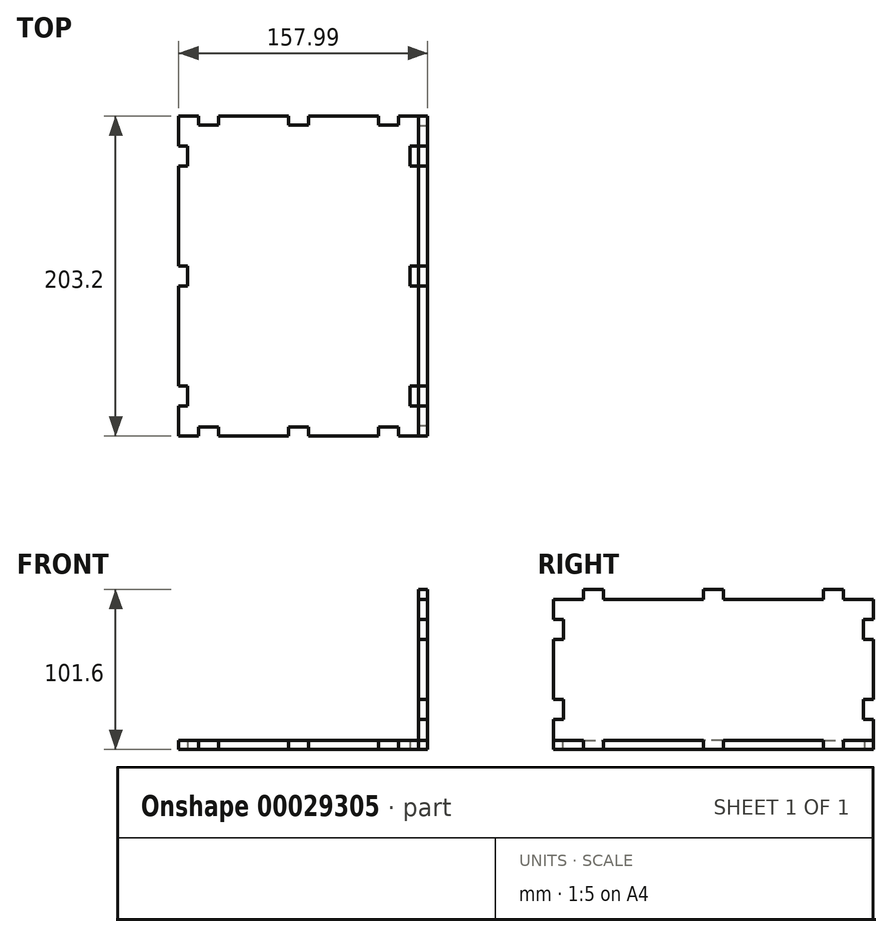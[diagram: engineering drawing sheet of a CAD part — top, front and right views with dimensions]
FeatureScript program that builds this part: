
annotation { "Feature Type Name" : "Feature", "Feature Type Description" : "" }
export const myFeature = defineFeature(function(context is Context, id is Id, definition is map)
    precondition{}
    {
        {
            var Q0;
            Q0=qCreatedBy(makeId("Top.planeOp"),FACE);
            var sketch = newSketch(context, id + "F0", { "sketchPlane" : qUnion([Q0])});
            skLineSegment(sketch, "E0", {"start": v(0, -101.6) * mm, "end": v(0, 101.6) * mm, "construction": true});
            skLineSegment(sketch, "E1", {"start": v(-76.2, 0) * mm, "end": v(76.2, 0) * mm, "construction": true});
            skLineSegment(sketch, "E2.0", {"start": v(38.1, -101.6) * mm, "end": v(38.1, 101.6) * mm, "construction": true});
            skLineSegment(sketch, "E3.0", {"start": v(76.2, -101.6) * mm, "end": v(76.2, -82.55) * mm, "construction": true});
            skLineSegment(sketch, "E4.0", {"start": v(-38.1, -101.6) * mm, "end": v(-38.1, 101.6) * mm, "construction": true});
            skLineSegment(sketch, "E5.0", {"start": v(-76.2, -101.6) * mm, "end": v(-76.2, 76.2) * mm, "construction": true});
            skLineSegment(sketch, "E6.0", {"start": v(-76.2, -50.8) * mm, "end": v(76.2, -50.8) * mm, "construction": true});
            skLineSegment(sketch, "E7.0", {"start": v(-76.2, -101.6) * mm, "end": v(-63.5, -101.6) * mm, "construction": true});
            skLineSegment(sketch, "E8.0", {"start": v(-76.2, 50.8) * mm, "end": v(76.2, 50.8) * mm, "construction": true});
            skLineSegment(sketch, "E9.0", {"start": v(-76.2, 101.6) * mm, "end": v(76.2, 101.6) * mm, "construction": true});
            skLineSegment(sketch, "E10.bottom", {"start": v(-76.2, -101.6) * mm, "end": v(-63.5, -101.6) * mm});
            skLineSegment(sketch, "E10.top", {"start": v(-76.2, 101.6) * mm, "end": v(-63.5, 101.6) * mm});
            skLineSegment(sketch, "E10.left", {"start": v(-76.2, -101.6) * mm, "end": v(-76.2, -82.55) * mm});
            skLineSegment(sketch, "E10.right", {"start": v(76.2, -101.6) * mm, "end": v(76.2, -82.55) * mm});
            skLineSegment(sketch, "E11.0", {"start": v(-57.15, -101.6) * mm, "end": v(-57.15, 101.6) * mm, "construction": true});
            skLineSegment(sketch, "E12.0", {"start": v(57.15, -101.6) * mm, "end": v(57.15, 101.6) * mm, "construction": true});
            skLineSegment(sketch, "E13.0", {"start": v(-76.2, -76.2) * mm, "end": v(76.2, -76.2) * mm, "construction": true});
            skLineSegment(sketch, "E14.0", {"start": v(-76.2, 76.2) * mm, "end": v(76.2, 76.2) * mm, "construction": true});
            skLineSegment(sketch, "E15.0", {"start": v(-76.2, -69.85) * mm, "end": v(76.2, -69.85) * mm, "construction": true});
            skLineSegment(sketch, "E16.0", {"start": v(-76.2, -82.55) * mm, "end": v(76.2, -82.55) * mm, "construction": true});
            skLineSegment(sketch, "E17.0", {"start": v(-70.61, -101.6) * mm, "end": v(-70.61, 101.6) * mm, "construction": true});
            skLineSegment(sketch, "E18.0", {"start": v(-76.2, -96.01) * mm, "end": v(76.2, -96.01) * mm, "construction": true});
            skLineSegment(sketch, "E19.0", {"start": v(-76.2, 96.01) * mm, "end": v(76.2, 96.01) * mm, "construction": true});
            skLineSegment(sketch, "E20.0", {"start": v(70.61, -101.6) * mm, "end": v(70.61, 101.6) * mm, "construction": true});
            skLineSegment(sketch, "E21", {"start": v(-76.2, -82.55) * mm, "end": v(-70.61, -82.55) * mm});
            skLineSegment(sketch, "E22", {"start": v(-70.61, -82.55) * mm, "end": v(-70.61, -69.85) * mm});
            skLineSegment(sketch, "E23", {"start": v(-70.61, -69.85) * mm, "end": v(-76.2, -69.85) * mm});
            skLineSegment(sketch, "E24", {"start": v(76.2, -82.55) * mm, "end": v(70.61, -82.55) * mm});
            skLineSegment(sketch, "E25", {"start": v(70.61, -82.55) * mm, "end": v(70.61, -69.85) * mm});
            skLineSegment(sketch, "E26", {"start": v(70.61, -69.85) * mm, "end": v(76.2, -69.85) * mm});
            skLineSegment(sketch, "E27.0", {"start": v(-76.2, 6.35) * mm, "end": v(76.2, 6.35) * mm, "construction": true});
            skLineSegment(sketch, "E28.0", {"start": v(-76.2, -6.35) * mm, "end": v(76.2, -6.35) * mm, "construction": true});
            skLineSegment(sketch, "E29", {"start": v(-76.2, -6.35) * mm, "end": v(-70.61, -6.35) * mm});
            skLineSegment(sketch, "E30.0", {"start": v(-76.2, 82.55) * mm, "end": v(76.2, 82.55) * mm, "construction": true});
            skLineSegment(sketch, "E31.0", {"start": v(-76.2, 69.85) * mm, "end": v(76.2, 69.85) * mm, "construction": true});
            skLineSegment(sketch, "E32", {"start": v(-70.61, -6.35) * mm, "end": v(-70.61, 6.35) * mm});
            skLineSegment(sketch, "E33", {"start": v(-70.61, 6.35) * mm, "end": v(-76.2, 6.35) * mm});
            skLineSegment(sketch, "E34", {"start": v(-76.2, 69.85) * mm, "end": v(-70.61, 69.85) * mm});
            skLineSegment(sketch, "E35", {"start": v(-70.61, 69.85) * mm, "end": v(-70.61, 82.55) * mm});
            skLineSegment(sketch, "E36", {"start": v(-70.61, 82.55) * mm, "end": v(-76.2, 82.55) * mm});
            skLineSegment(sketch, "E37", {"start": v(76.2, 69.85) * mm, "end": v(70.61, 69.85) * mm});
            skLineSegment(sketch, "E38", {"start": v(70.61, 69.85) * mm, "end": v(70.61, 82.55) * mm});
            skLineSegment(sketch, "E39", {"start": v(70.61, 82.55) * mm, "end": v(76.2, 82.55) * mm});
            skLineSegment(sketch, "E40", {"start": v(76.2, 6.35) * mm, "end": v(70.61, 6.35) * mm});
            skLineSegment(sketch, "E41", {"start": v(70.61, 6.35) * mm, "end": v(70.61, -6.35) * mm});
            skLineSegment(sketch, "E42", {"start": v(70.61, -6.35) * mm, "end": v(76.2, -6.35) * mm});
            skLineSegment(sketch, "E43.0", {"start": v(-63.5, -101.6) * mm, "end": v(-63.5, 101.6) * mm, "construction": true});
            skLineSegment(sketch, "E44.0", {"start": v(-50.8, -101.6) * mm, "end": v(-50.8, 101.6) * mm, "construction": true});
            skLineSegment(sketch, "E45.0", {"start": v(-6.35, -101.6) * mm, "end": v(-6.35, 101.6) * mm, "construction": true});
            skLineSegment(sketch, "E46.0", {"start": v(6.35, -101.6) * mm, "end": v(6.35, 101.6) * mm, "construction": true});
            skLineSegment(sketch, "E47.0", {"start": v(50.8, -101.6) * mm, "end": v(50.8, 101.6) * mm, "construction": true});
            skLineSegment(sketch, "E48.0", {"start": v(63.5, -101.6) * mm, "end": v(63.5, 101.6) * mm, "construction": true});
            skLineSegment(sketch, "E49", {"start": v(-63.5, -101.6) * mm, "end": v(-63.5, -96.01) * mm});
            skLineSegment(sketch, "E50", {"start": v(-63.5, -96.01) * mm, "end": v(-50.8, -96.01) * mm});
            skLineSegment(sketch, "E51", {"start": v(-50.8, -96.01) * mm, "end": v(-50.8, -101.6) * mm});
            skLineSegment(sketch, "E52", {"start": v(-6.35, -101.6) * mm, "end": v(-6.35, -96.01) * mm});
            skLineSegment(sketch, "E53", {"start": v(-6.35, -96.01) * mm, "end": v(6.35, -96.01) * mm});
            skLineSegment(sketch, "E54", {"start": v(6.35, -96.01) * mm, "end": v(6.35, -101.6) * mm});
            skLineSegment(sketch, "E55", {"start": v(50.8, -101.6) * mm, "end": v(50.8, -96.01) * mm});
            skLineSegment(sketch, "E56", {"start": v(50.8, -96.01) * mm, "end": v(63.5, -96.01) * mm});
            skLineSegment(sketch, "E57", {"start": v(63.5, -96.01) * mm, "end": v(63.5, -101.6) * mm});
            skLineSegment(sketch, "E58.trimOffspring", {"start": v(63.5, -101.6) * mm, "end": v(76.2, -101.6) * mm});
            skLineSegment(sketch, "E59.trimOffspring", {"start": v(76.2, -69.85) * mm, "end": v(76.2, -6.35) * mm});
            skLineSegment(sketch, "E60.trimOffspring", {"start": v(76.2, -69.85) * mm, "end": v(76.2, -6.35) * mm, "construction": true});
            skLineSegment(sketch, "E61.trimOffspring", {"start": v(76.2, 6.35) * mm, "end": v(76.2, 69.85) * mm});
            skLineSegment(sketch, "E62.trimOffspring", {"start": v(76.2, 6.35) * mm, "end": v(76.2, 69.85) * mm, "construction": true});
            skLineSegment(sketch, "E63.trimOffspring", {"start": v(76.2, 82.55) * mm, "end": v(76.2, 101.6) * mm});
            skLineSegment(sketch, "E64.trimOffspring", {"start": v(76.2, 82.55) * mm, "end": v(76.2, 101.6) * mm, "construction": true});
            skLineSegment(sketch, "E65.trimOffspring", {"start": v(-76.2, 82.55) * mm, "end": v(-76.2, 101.6) * mm});
            skLineSegment(sketch, "E66.trimOffspring", {"start": v(-76.2, 82.55) * mm, "end": v(-76.2, 101.6) * mm, "construction": true});
            skLineSegment(sketch, "E67.trimOffspring", {"start": v(-76.2, 6.35) * mm, "end": v(-76.2, 69.85) * mm});
            skLineSegment(sketch, "E68.trimOffspring", {"start": v(-76.2, -69.85) * mm, "end": v(-76.2, -6.35) * mm});
            skLineSegment(sketch, "E69.trimOffspring", {"start": v(-50.8, -101.6) * mm, "end": v(-6.35, -101.6) * mm});
            skLineSegment(sketch, "E70.trimOffspring", {"start": v(-57.15, -101.6) * mm, "end": v(76.2, -101.6) * mm, "construction": true});
            skLineSegment(sketch, "E71.trimOffspring", {"start": v(6.35, -101.6) * mm, "end": v(50.8, -101.6) * mm});
            skLineSegment(sketch, "E72", {"start": v(-63.5, 101.6) * mm, "end": v(-63.5, 96.01) * mm});
            skLineSegment(sketch, "E73", {"start": v(-63.5, 96.01) * mm, "end": v(-50.8, 96.01) * mm});
            skLineSegment(sketch, "E74", {"start": v(-50.8, 96.01) * mm, "end": v(-50.8, 101.6) * mm});
            skLineSegment(sketch, "E75", {"start": v(-6.35, 101.6) * mm, "end": v(-6.35, 96.01) * mm});
            skLineSegment(sketch, "E76", {"start": v(-6.35, 96.01) * mm, "end": v(6.35, 96.01) * mm});
            skLineSegment(sketch, "E77", {"start": v(6.35, 96.01) * mm, "end": v(6.35, 101.6) * mm});
            skLineSegment(sketch, "E78", {"start": v(50.8, 101.6) * mm, "end": v(50.8, 96.01) * mm});
            skLineSegment(sketch, "E79", {"start": v(50.8, 96.01) * mm, "end": v(63.5, 96.01) * mm});
            skLineSegment(sketch, "E80", {"start": v(63.5, 96.01) * mm, "end": v(63.5, 101.6) * mm});
            skLineSegment(sketch, "E81.trimOffspring", {"start": v(63.5, 101.6) * mm, "end": v(76.2, 101.6) * mm});
            skLineSegment(sketch, "E82.trimOffspring", {"start": v(6.35, 101.6) * mm, "end": v(50.8, 101.6) * mm});
            skLineSegment(sketch, "E83.trimOffspring", {"start": v(-50.8, 101.6) * mm, "end": v(-6.35, 101.6) * mm});
            skSolve(sketch);
        }
        {
            var Q0;
            Q0=makeQuery(id+"F0.imprint","IMPRINT",FACE,{"disambiguationData":[TD([[makeQuery(id+"F0.imprint","IMPRINT",EDGE,{"derivedFrom":sQuery(id+"F0.wireOp",EDGE,"E10.bottom")}),1.0]])]});
            extrude(context, id + "F1", {"entities" : qUnion([Q0]), "depth" : 5.6 * mm});
        }
        {
            var Q0;
            Q0=qCreatedBy(makeId("Right.planeOp"),FACE);
            cPlane(context, id + "F2", {"entities" : qUnion([Q0]), "cplaneType" : CPlaneType.OFFSET, "offset" : 76.2 * mm, "width" : 152.4 * mm, "height" : 152.4 * mm});
        }
        {
            var Q0;
            Q0=qCreatedBy(id+"F2.planeOp",FACE);
            var sketch = newSketch(context, id + "F3", { "sketchPlane" : qUnion([Q0])});
            skLineSegment(sketch, "E84", {"start": v(0, 0) * mm, "end": v(0, 101.6) * mm, "construction": true});
            skLineSegment(sketch, "E85", {"start": v(0, 50.8) * mm, "end": v(-101.6, 50.8) * mm, "construction": true});
            skLineSegment(sketch, "E86", {"start": v(0, 50.8) * mm, "end": v(101.6, 50.8) * mm, "construction": true});
            skPoint(sketch, "E87.0", {"position": v(-76.2, 0) * mm});
            skPoint(sketch, "E88.0", {"position": v(76.2, 0) * mm});
            skLineSegment(sketch, "E89.0", {"start": v(0, 101.6) * mm, "end": v(-101.6, 101.6) * mm, "construction": true});
            skLineSegment(sketch, "E90.0", {"start": v(0, 101.6) * mm, "end": v(101.6, 101.6) * mm, "construction": true});
            skLineSegment(sketch, "E91.0", {"start": v(101.6, 0) * mm, "end": v(101.6, 101.6) * mm, "construction": true});
            skLineSegment(sketch, "E92.0", {"start": v(-101.6, 0) * mm, "end": v(-101.6, 101.6) * mm, "construction": true});
            skLineSegment(sketch, "E93.0", {"start": v(0, 0) * mm, "end": v(-101.6, 0) * mm, "construction": true});
            skLineSegment(sketch, "E94.0", {"start": v(0, 0) * mm, "end": v(101.6, 0) * mm, "construction": true});
            skLineSegment(sketch, "E95.0", {"start": v(0, 25.4) * mm, "end": v(101.6, 25.4) * mm, "construction": true});
            skLineSegment(sketch, "E96.0", {"start": v(0, 76.2) * mm, "end": v(101.6, 76.2) * mm, "construction": true});
            skLineSegment(sketch, "E97.0", {"start": v(0, 76.2) * mm, "end": v(-101.6, 76.2) * mm, "construction": true});
            skLineSegment(sketch, "E98.0", {"start": v(0, 25.4) * mm, "end": v(-101.6, 25.4) * mm, "construction": true});
            skLineSegment(sketch, "E99.0", {"start": v(-101.6, 5.59) * mm, "end": v(-82.55, 5.59) * mm});
            skLineSegment(sketch, "E100.0", {"start": v(-82.55, 5.59) * mm, "end": v(-82.55, 0) * mm});
            skLineSegment(sketch, "E101.0", {"start": v(-69.85, 5.59) * mm, "end": v(-69.85, 0) * mm});
            skLineSegment(sketch, "E102.0", {"start": v(-69.85, 5.59) * mm, "end": v(-6.35, 5.59) * mm});
            skLineSegment(sketch, "E103.0", {"start": v(-6.35, 5.59) * mm, "end": v(-6.35, 0) * mm});
            skLineSegment(sketch, "E104.0", {"start": v(6.35, 5.59) * mm, "end": v(6.35, 0) * mm});
            skLineSegment(sketch, "E105.0", {"start": v(6.35, 5.59) * mm, "end": v(69.85, 5.59) * mm});
            skLineSegment(sketch, "E106.0", {"start": v(69.85, 5.59) * mm, "end": v(69.85, 0) * mm});
            skLineSegment(sketch, "E107.0", {"start": v(82.55, 5.59) * mm, "end": v(82.55, 0) * mm});
            skLineSegment(sketch, "E108.0", {"start": v(82.55, 5.59) * mm, "end": v(101.6, 5.59) * mm});
            skLineSegment(sketch, "E109.MirrorCS", {"start": v(-82.55, 96.01) * mm, "end": v(-82.55, 101.6) * mm});
            skLineSegment(sketch, "E110.MirrorCS", {"start": v(-69.85, 96.01) * mm, "end": v(-69.85, 101.6) * mm});
            skLineSegment(sketch, "E111.MirrorCS", {"start": v(-6.35, 96.01) * mm, "end": v(-6.35, 101.6) * mm});
            skLineSegment(sketch, "E112.MirrorCS", {"start": v(6.35, 96.01) * mm, "end": v(6.35, 101.6) * mm});
            skLineSegment(sketch, "E113.MirrorCS", {"start": v(69.85, 96.01) * mm, "end": v(69.85, 101.6) * mm});
            skLineSegment(sketch, "E114.MirrorCS", {"start": v(82.55, 96.01) * mm, "end": v(82.55, 101.6) * mm});
            skLineSegment(sketch, "E115", {"start": v(-76.2, 0) * mm, "end": v(-76.2, 101.6) * mm, "construction": true});
            skLineSegment(sketch, "E116", {"start": v(76.2, 0) * mm, "end": v(76.2, 101.6) * mm, "construction": true});
            skLineSegment(sketch, "E117", {"start": v(-82.55, 101.6) * mm, "end": v(-69.85, 101.6) * mm});
            skLineSegment(sketch, "E118", {"start": v(-6.35, 101.6) * mm, "end": v(6.35, 101.6) * mm});
            skLineSegment(sketch, "E119", {"start": v(69.85, 101.6) * mm, "end": v(82.55, 101.6) * mm});
            skLineSegment(sketch, "E120.0", {"start": v(0, 31.75) * mm, "end": v(-101.6, 31.75) * mm, "construction": true});
            skLineSegment(sketch, "E121.0", {"start": v(0, 19.05) * mm, "end": v(-101.6, 19.05) * mm, "construction": true});
            skLineSegment(sketch, "E122.0", {"start": v(-95.25, 0) * mm, "end": v(-95.25, 101.6) * mm, "construction": true});
            skLineSegment(sketch, "E123.0", {"start": v(95.25, 0) * mm, "end": v(95.25, 101.6) * mm, "construction": true});
            skLineSegment(sketch, "E124.0", {"start": v(0, 69.85) * mm, "end": v(-101.6, 69.85) * mm, "construction": true});
            skLineSegment(sketch, "E125.0", {"start": v(0, 82.55) * mm, "end": v(-101.6, 82.55) * mm, "construction": true});
            skLineSegment(sketch, "E126.0", {"start": v(0, 82.55) * mm, "end": v(101.6, 82.55) * mm, "construction": true});
            skLineSegment(sketch, "E127.0", {"start": v(0, 69.85) * mm, "end": v(101.6, 69.85) * mm, "construction": true});
            skLineSegment(sketch, "E128.0", {"start": v(0, 19.05) * mm, "end": v(101.6, 19.05) * mm, "construction": true});
            skLineSegment(sketch, "E129.0", {"start": v(0, 31.75) * mm, "end": v(101.6, 31.75) * mm, "construction": true});
            skLineSegment(sketch, "E130", {"start": v(-101.6, 96.01) * mm, "end": v(-101.6, 82.55) * mm});
            skLineSegment(sketch, "E131", {"start": v(-101.6, 82.55) * mm, "end": v(-95.25, 82.55) * mm});
            skLineSegment(sketch, "E132", {"start": v(-95.25, 82.55) * mm, "end": v(-95.25, 69.85) * mm});
            skLineSegment(sketch, "E133", {"start": v(-95.25, 69.85) * mm, "end": v(-101.6, 69.85) * mm});
            skLineSegment(sketch, "E134", {"start": v(-101.6, 69.85) * mm, "end": v(-101.6, 31.75) * mm});
            skLineSegment(sketch, "E135", {"start": v(-101.6, 31.75) * mm, "end": v(-95.25, 31.75) * mm});
            skLineSegment(sketch, "E136", {"start": v(-95.25, 31.75) * mm, "end": v(-95.25, 19.05) * mm});
            skLineSegment(sketch, "E137", {"start": v(-95.25, 19.05) * mm, "end": v(-101.6, 19.05) * mm});
            skLineSegment(sketch, "E138", {"start": v(-101.6, 19.05) * mm, "end": v(-101.6, 5.59) * mm});
            skLineSegment(sketch, "E139", {"start": v(101.6, 5.59) * mm, "end": v(101.6, 19.05) * mm});
            skLineSegment(sketch, "E140", {"start": v(95.25, 19.05) * mm, "end": v(95.25, 31.75) * mm});
            skLineSegment(sketch, "E141", {"start": v(95.25, 31.75) * mm, "end": v(101.6, 31.75) * mm});
            skLineSegment(sketch, "E142", {"start": v(101.6, 31.75) * mm, "end": v(101.6, 69.85) * mm});
            skLineSegment(sketch, "E143", {"start": v(95.25, 69.85) * mm, "end": v(95.25, 82.55) * mm});
            skLineSegment(sketch, "E144", {"start": v(95.25, 82.55) * mm, "end": v(101.6, 82.55) * mm});
            skLineSegment(sketch, "E145", {"start": v(101.6, 82.55) * mm, "end": v(101.6, 95.25) * mm});
            skLineSegment(sketch, "E146", {"start": v(101.6, 69.85) * mm, "end": v(95.25, 69.85) * mm});
            skLineSegment(sketch, "E147", {"start": v(101.6, 19.05) * mm, "end": v(95.25, 19.05) * mm});
            skLineSegment(sketch, "E148", {"start": v(-82.55, 0) * mm, "end": v(-69.85, 0) * mm});
            skLineSegment(sketch, "E149", {"start": v(-6.35, 0) * mm, "end": v(6.35, 0) * mm});
            skLineSegment(sketch, "E150", {"start": v(69.85, 0) * mm, "end": v(82.55, 0) * mm});
            skLineSegment(sketch, "E151.0", {"start": v(-101.6, 95.25) * mm, "end": v(101.6, 95.25) * mm, "construction": true});
            skLineSegment(sketch, "E152", {"start": v(-101.6, 95.25) * mm, "end": v(-82.55, 95.25) * mm});
            skLineSegment(sketch, "E153", {"start": v(-82.55, 95.25) * mm, "end": v(-82.55, 96.01) * mm});
            skLineSegment(sketch, "E154", {"start": v(-69.85, 96.01) * mm, "end": v(-69.85, 95.25) * mm});
            skLineSegment(sketch, "E155", {"start": v(-69.85, 95.25) * mm, "end": v(-6.35, 95.25) * mm});
            skLineSegment(sketch, "E156", {"start": v(-6.35, 95.25) * mm, "end": v(-6.35, 96.01) * mm});
            skLineSegment(sketch, "E157", {"start": v(6.35, 96.01) * mm, "end": v(6.35, 95.25) * mm});
            skLineSegment(sketch, "E158", {"start": v(6.35, 95.25) * mm, "end": v(69.85, 95.25) * mm});
            skLineSegment(sketch, "E159", {"start": v(69.85, 95.25) * mm, "end": v(69.85, 96.01) * mm});
            skLineSegment(sketch, "E160", {"start": v(82.55, 96.01) * mm, "end": v(82.55, 95.25) * mm});
            skLineSegment(sketch, "E161", {"start": v(82.55, 95.25) * mm, "end": v(101.6, 95.25) * mm});
            skPoint(sketch, "E162.orphan", {"position": v(101.6, 96.01) * mm});
            skSolve(sketch);
        }
        {
            var Q0;
            Q0=makeQuery(id+"F3.imprint","IMPRINT",FACE,{"disambiguationData":[TD([[makeQuery(id+"F3.imprint","IMPRINT",EDGE,{"derivedFrom":sQuery(id+"F3.wireOp",EDGE,"E99.0")}),1.0]])]});
            extrude(context, id + "F4", {"entities" : qUnion([Q0]), "depth" : 5.6 * mm});
        }
    });
